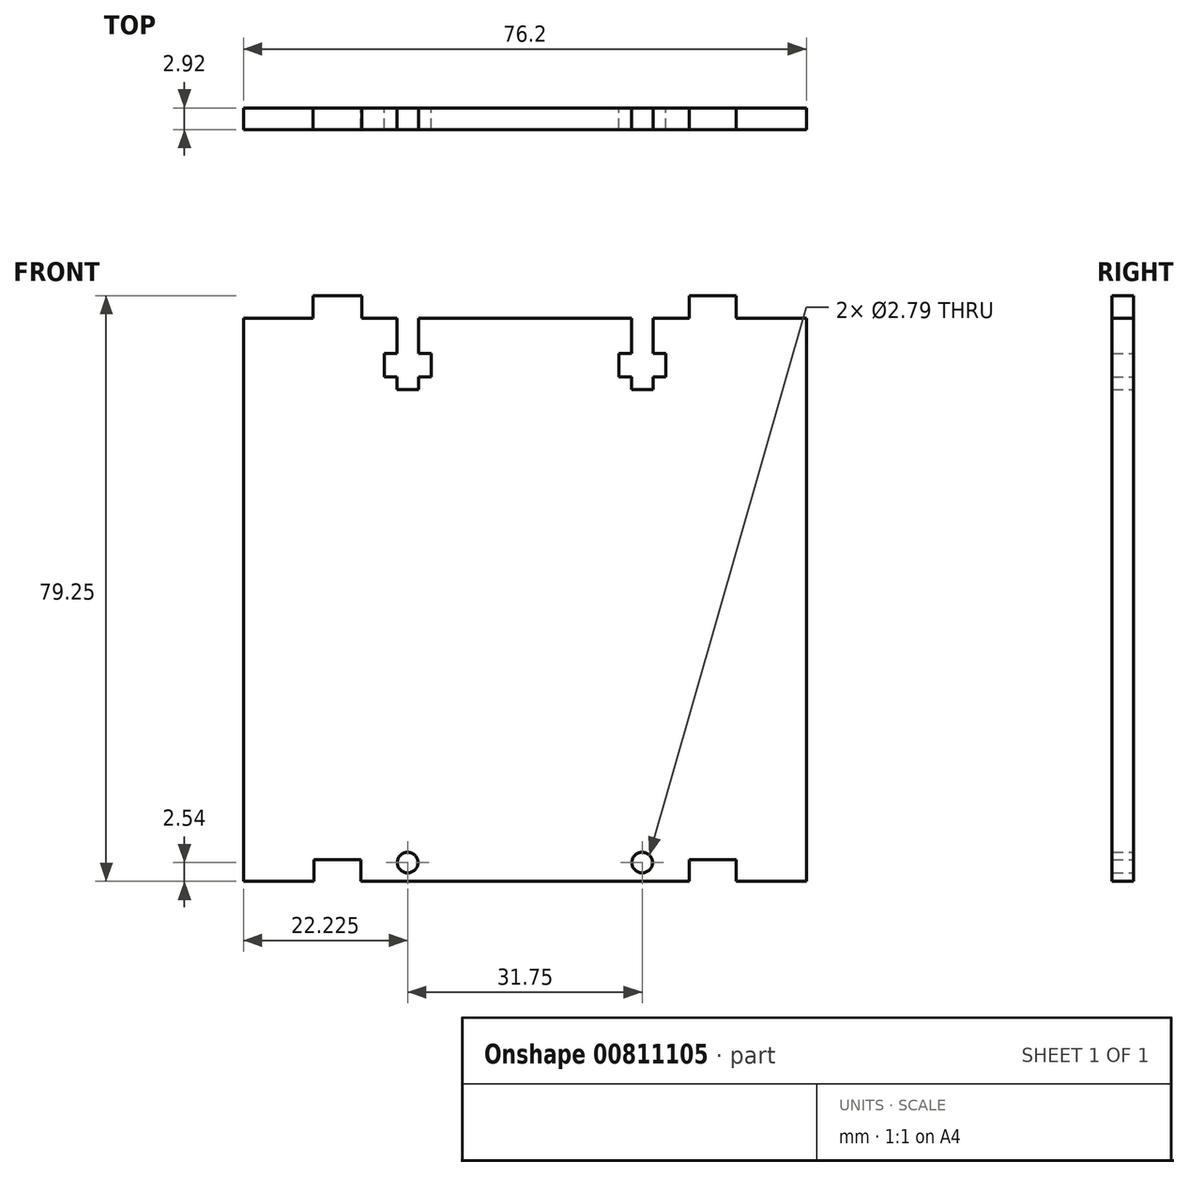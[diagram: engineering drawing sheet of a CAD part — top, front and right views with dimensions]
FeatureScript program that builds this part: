
annotation { "Feature Type Name" : "Feature", "Feature Type Description" : "" }
export const myFeature = defineFeature(function(context is Context, id is Id, definition is map)
    precondition{}
    {
        {
            var Q0;
            Q0=qCreatedBy(makeId("Front.planeOp"),FACE);
            var sketch = newSketch(context, id + "F0", { "sketchPlane" : qUnion([Q0])});
            skLineSegment(sketch, "E0.bottom", {"start": v(0, 0) * mm, "end": v(76.2, 0) * mm});
            skLineSegment(sketch, "E0.top", {"start": v(0, 76.2) * mm, "end": v(76.2, 76.2) * mm});
            skLineSegment(sketch, "E0.left", {"start": v(0, 0) * mm, "end": v(0, 76.2) * mm});
            skLineSegment(sketch, "E0.right", {"start": v(76.2, 0) * mm, "end": v(76.2, 76.2) * mm});
            skLineSegment(sketch, "E1", {"start": v(0, 0) * mm, "end": v(12.7, 0) * mm});
            skLineSegment(sketch, "E2.bottom", {"start": v(15.88, 2.92) * mm, "end": v(9.53, 2.92) * mm});
            skLineSegment(sketch, "E2.top", {"start": v(15.88, -2.92) * mm, "end": v(9.53, -2.92) * mm});
            skLineSegment(sketch, "E2.left", {"start": v(15.88, 2.92) * mm, "end": v(15.88, -2.92) * mm});
            skLineSegment(sketch, "E2.right", {"start": v(9.53, 2.92) * mm, "end": v(9.53, -2.92) * mm});
            skPoint(sketch, "E2.middle", {"position": v(12.7, 0) * mm});
            skLineSegment(sketch, "E3", {"start": v(76.2, 0) * mm, "end": v(63.5, 0) * mm});
            skLineSegment(sketch, "E4", {"start": v(0, 76.2) * mm, "end": v(12.7, 76.2) * mm});
            skLineSegment(sketch, "E5", {"start": v(76.2, 76.2) * mm, "end": v(63.5, 76.2) * mm});
            skLineSegment(sketch, "E6.bottom", {"start": v(16, 79.25) * mm, "end": v(9.4, 79.25) * mm});
            skLineSegment(sketch, "E6.top", {"start": v(16, 73.15) * mm, "end": v(9.4, 73.15) * mm});
            skLineSegment(sketch, "E6.left", {"start": v(16, 79.25) * mm, "end": v(16, 73.15) * mm});
            skLineSegment(sketch, "E6.right", {"start": v(9.4, 79.25) * mm, "end": v(9.4, 73.15) * mm});
            skPoint(sketch, "E6.middle", {"position": v(12.7, 76.2) * mm});
            skLineSegment(sketch, "E7.bottom", {"start": v(60.33, 79.25) * mm, "end": v(66.68, 79.25) * mm});
            skLineSegment(sketch, "E7.top", {"start": v(60.33, 73.15) * mm, "end": v(66.68, 73.15) * mm});
            skLineSegment(sketch, "E7.left", {"start": v(60.33, 79.25) * mm, "end": v(60.33, 73.15) * mm});
            skLineSegment(sketch, "E7.right", {"start": v(66.68, 79.25) * mm, "end": v(66.68, 73.15) * mm});
            skPoint(sketch, "E7.middle", {"position": v(63.5, 76.2) * mm});
            skLineSegment(sketch, "E8.bottom", {"start": v(60.33, 2.92) * mm, "end": v(66.67, 2.92) * mm});
            skLineSegment(sketch, "E8.top", {"start": v(60.33, -2.92) * mm, "end": v(66.67, -2.92) * mm});
            skLineSegment(sketch, "E8.left", {"start": v(60.33, 2.92) * mm, "end": v(60.33, -2.92) * mm});
            skLineSegment(sketch, "E8.right", {"start": v(66.67, 2.92) * mm, "end": v(66.67, -2.92) * mm});
            skPoint(sketch, "E8.middle", {"position": v(63.5, 0) * mm});
            skCircle(sketch, "E9", {"center": v(53.98, 2.54) * mm, "radius": 1.4 * mm});
            skLineSegment(sketch, "E10", {"start": v(38.1, 0) * mm, "end": v(38.1, 76.2) * mm});
            skLineSegment(sketch, "E11", {"start": v(60.32, 76.2) * mm, "end": v(53.97, 76.2) * mm});
            skLineSegment(sketch, "E12.bottom", {"start": v(55.44, 66.55) * mm, "end": v(52.51, 66.55) * mm});
            skLineSegment(sketch, "E12.top", {"start": v(55.44, 85.85) * mm, "end": v(52.51, 85.85) * mm});
            skLineSegment(sketch, "E12.left", {"start": v(55.44, 66.55) * mm, "end": v(55.44, 85.85) * mm});
            skLineSegment(sketch, "E12.right", {"start": v(52.51, 66.55) * mm, "end": v(52.51, 85.85) * mm});
            skPoint(sketch, "E12.middle", {"position": v(53.97, 76.2) * mm});
            skLineSegment(sketch, "E13", {"start": v(53.98, 76.2) * mm, "end": v(53.98, 66.55) * mm});
            skLineSegment(sketch, "E14.bottom", {"start": v(57.15, 71.44) * mm, "end": v(50.8, 71.44) * mm});
            skLineSegment(sketch, "E14.top", {"start": v(57.15, 68.26) * mm, "end": v(50.8, 68.26) * mm});
            skLineSegment(sketch, "E14.left", {"start": v(57.15, 71.44) * mm, "end": v(57.15, 68.26) * mm});
            skLineSegment(sketch, "E14.right", {"start": v(50.8, 71.44) * mm, "end": v(50.8, 68.26) * mm});
            skPoint(sketch, "E14.middle", {"position": v(53.97, 69.85) * mm});
            skCircle(sketch, "E15.MirrorC", {"center": v(22.23, 2.54) * mm, "radius": 1.4 * mm});
            skLineSegment(sketch, "E16.MirrorCS", {"start": v(19.05, 68.26) * mm, "end": v(25.4, 68.26) * mm});
            skLineSegment(sketch, "E17.MirrorCS", {"start": v(22.23, 76.2) * mm, "end": v(22.23, 66.55) * mm});
            skLineSegment(sketch, "E18.MirrorCS", {"start": v(23.69, 66.55) * mm, "end": v(23.69, 85.85) * mm});
            skPoint(sketch, "E19.MirrorP", {"position": v(22.23, 69.85) * mm});
            skLineSegment(sketch, "E20.MirrorCS", {"start": v(19.05, 71.44) * mm, "end": v(19.05, 68.26) * mm});
            skLineSegment(sketch, "E21.MirrorCS", {"start": v(20.76, 85.85) * mm, "end": v(23.69, 85.85) * mm});
            skPoint(sketch, "E22.MirrorP", {"position": v(22.22, 76.2) * mm});
            skLineSegment(sketch, "E23.MirrorCS", {"start": v(20.76, 66.55) * mm, "end": v(20.76, 85.85) * mm});
            skLineSegment(sketch, "E24.MirrorCS", {"start": v(25.4, 71.44) * mm, "end": v(25.4, 68.26) * mm});
            skLineSegment(sketch, "E25.MirrorCS", {"start": v(19.05, 71.44) * mm, "end": v(25.4, 71.44) * mm});
            skLineSegment(sketch, "E26.MirrorCS", {"start": v(20.76, 66.55) * mm, "end": v(23.69, 66.55) * mm});
            skSolve(sketch);
        }
        {
            var Q0;
            {var subQ23=sQuery(id+"F0.wireOp",EDGE,"E0.right");Q0=makeQuery(id+"F0.imprint","IMPRINT",FACE,{"disambiguationData":[TD([[makeQuery(id+"F0.imprint","IMPRINT",EDGE,{"derivedFrom":subQ23}),1.0]])]});}
            var Q1;
            {var subQ28=sQuery(id+"F0.wireOp",EDGE,"E0.left");Q1=makeQuery(id+"F0.imprint","IMPRINT",FACE,{"disambiguationData":[TD([[makeQuery(id+"F0.imprint","IMPRINT",EDGE,{"derivedFrom":subQ28}),-1.0]])]});}
            var Q2;
            {var subQ0=sQuery(id+"F0.wireOp",EDGE,"E7.top");Q2=makeQuery(id+"F0.imprint","IMPRINT",FACE,{"disambiguationData":[TD([[makeQuery(id+"F0.imprint","IMPRINT",EDGE,{"derivedFrom":subQ0}),1.0]])]});}
            var Q3;
            {var subQ0=sQuery(id+"F0.wireOp",EDGE,"E7.bottom");Q3=makeQuery(id+"F0.imprint","IMPRINT",FACE,{"disambiguationData":[TD([[makeQuery(id+"F0.imprint","IMPRINT",EDGE,{"derivedFrom":subQ0}),-1.0]])]});}
            var Q4;
            {var subQ1=sQuery(id+"F0.wireOp",EDGE,"E6.top");Q4=makeQuery(id+"F0.imprint","IMPRINT",FACE,{"disambiguationData":[TD([[makeQuery(id+"F0.imprint","IMPRINT",EDGE,{"derivedFrom":subQ1}),-1.0]])]});}
            var Q5;
            {var subQ0=sQuery(id+"F0.wireOp",EDGE,"E6.bottom");Q5=makeQuery(id+"F0.imprint","IMPRINT",FACE,{"disambiguationData":[TD([[makeQuery(id+"F0.imprint","IMPRINT",EDGE,{"derivedFrom":subQ0}),1.0]])]});}
            extrude(context, id + "F1", {"entities" : qUnion([Q0, Q1, Q2, Q3, Q4, Q5]), "depth" : 2.92 * mm, "offsetDistance" : 25.4 * mm});
        }
    });
